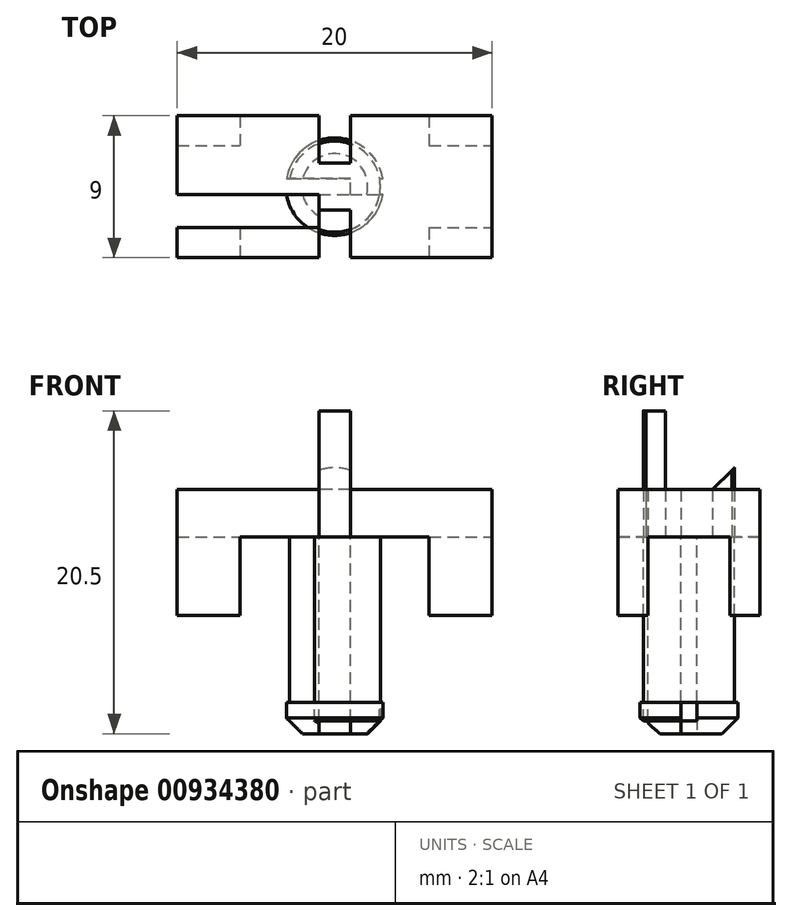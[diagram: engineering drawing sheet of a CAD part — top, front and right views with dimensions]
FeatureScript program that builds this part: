
annotation { "Feature Type Name" : "Feature", "Feature Type Description" : "" }
export const myFeature = defineFeature(function(context is Context, id is Id, definition is map)
    precondition{}
    {
        {
            var Q0;
            Q0=qCreatedBy(makeId("Top.planeOp"),FACE);
            var sketch = newSketch(context, id + "F0", { "sketchPlane" : qUnion([Q0])});
            skCircle(sketch, "E0", {"center": v(0, 0) * mm, "radius": 2.9 * mm});
            skLineSegment(sketch, "E1", {"start": v(-15.02, 0) * mm, "end": v(15.02, 0) * mm, "construction": true});
            skLineSegment(sketch, "E2.0", {"start": v(-15.02, -0.5) * mm, "end": v(15.02, -0.5) * mm});
            skLineSegment(sketch, "E3.0", {"start": v(-15.02, 0.5) * mm, "end": v(15.02, 0.5) * mm});
            skLineSegment(sketch, "E4.bottom", {"start": v(10, -4.5) * mm, "end": v(-10, -4.5) * mm});
            skLineSegment(sketch, "E4.top", {"start": v(10, 4.5) * mm, "end": v(-10, 4.5) * mm});
            skLineSegment(sketch, "E4.left", {"start": v(10, -4.5) * mm, "end": v(10, 4.5) * mm});
            skLineSegment(sketch, "E4.right", {"start": v(-10, -4.5) * mm, "end": v(-10, 4.5) * mm});
            skLineSegment(sketch, "E5.bottom", {"start": v(1, -4.5) * mm, "end": v(-1, -4.5) * mm});
            skLineSegment(sketch, "E5.top", {"start": v(1, 4.5) * mm, "end": v(-1, 4.5) * mm});
            skLineSegment(sketch, "E5.left", {"start": v(1, -4.5) * mm, "end": v(1, 4.5) * mm});
            skLineSegment(sketch, "E5.right", {"start": v(-1, -4.5) * mm, "end": v(-1, 4.5) * mm});
            skLineSegment(sketch, "E6", {"start": v(-1, 1.5) * mm, "end": v(1, 1.5) * mm});
            skLineSegment(sketch, "E7", {"start": v(-1, -1.5) * mm, "end": v(1, -1.5) * mm});
            skLineSegment(sketch, "E8", {"start": v(-10, 2.6) * mm, "end": v(10, 2.6) * mm});
            skLineSegment(sketch, "E9", {"start": v(-10, -2.6) * mm, "end": v(10, -2.6) * mm});
            skLineSegment(sketch, "E10", {"start": v(-6, 4.5) * mm, "end": v(-6, 2.6) * mm});
            skLineSegment(sketch, "E11", {"start": v(6, 4.5) * mm, "end": v(6, 2.6) * mm});
            skLineSegment(sketch, "E12", {"start": v(-6, -2.6) * mm, "end": v(-6, -4.5) * mm});
            skLineSegment(sketch, "E13", {"start": v(6, -2.6) * mm, "end": v(6, -4.5) * mm});
            skSolve(sketch);
        }
        {
            var Q0;
            {var subQ4=sQuery(id+"F0.wireOp",EDGE,"E8");var subQ6=sQuery(id+"F0.wireOp",EDGE,"E0");var subQ8=makeQuery(id+"F0.imprint","INTERSECT",VERTEX,{"disambiguationData":[OD(1.0)],"derivedFrom":[subQ6,subQ4]});Q0=makeQuery(id+"F0.imprint","IMPRINT",FACE,{"disambiguationData":[TD([[makeQuery(id+"F0.imprint","IMPRINT",EDGE,{"disambiguationData":[TD([[subQ8,-1.0]])],"derivedFrom":subQ6}),1.0]])]});}
            var Q1;
            {var subQ0=sQuery(id+"F0.wireOp",EDGE,"E6");Q1=makeQuery(id+"F0.imprint","IMPRINT",FACE,{"disambiguationData":[TD([[makeQuery(id+"F0.imprint","IMPRINT",EDGE,{"derivedFrom":subQ0}),1.0]])]});}
            var Q2;
            {var subQ5=sQuery(id+"F0.wireOp",EDGE,"E6");Q2=makeQuery(id+"F0.imprint","IMPRINT",FACE,{"disambiguationData":[TD([[makeQuery(id+"F0.imprint","IMPRINT",EDGE,{"derivedFrom":subQ5}),-1.0]])]});}
            var Q3;
            {var subQ2=sQuery(id+"F0.wireOp",EDGE,"E8");var subQ4=sQuery(id+"F0.wireOp",EDGE,"E0");var subQ5=makeQuery(id+"F0.imprint","INTERSECT",VERTEX,{"disambiguationData":[OD(0.0)],"derivedFrom":[subQ4,subQ2]});Q3=makeQuery(id+"F0.imprint","IMPRINT",FACE,{"disambiguationData":[TD([[makeQuery(id+"F0.imprint","IMPRINT",EDGE,{"disambiguationData":[TD([[subQ5,1.0]])],"derivedFrom":subQ4}),1.0]])]});}
            var Q4;
            {var subQ4=sQuery(id+"F0.wireOp",EDGE,"E9");var subQ6=sQuery(id+"F0.wireOp",EDGE,"E0");var subQ8=makeQuery(id+"F0.imprint","INTERSECT",VERTEX,{"disambiguationData":[OD(1.0)],"derivedFrom":[subQ6,subQ4]});Q4=makeQuery(id+"F0.imprint","IMPRINT",FACE,{"disambiguationData":[TD([[makeQuery(id+"F0.imprint","IMPRINT",EDGE,{"disambiguationData":[TD([[subQ8,-1.0]])],"derivedFrom":subQ6}),1.0]])]});}
            var Q5;
            {var subQ0=sQuery(id+"F0.wireOp",EDGE,"E7");Q5=makeQuery(id+"F0.imprint","IMPRINT",FACE,{"disambiguationData":[TD([[makeQuery(id+"F0.imprint","IMPRINT",EDGE,{"derivedFrom":subQ0}),-1.0]])]});}
            var Q6;
            {var subQ5=sQuery(id+"F0.wireOp",EDGE,"E7");Q6=makeQuery(id+"F0.imprint","IMPRINT",FACE,{"disambiguationData":[TD([[makeQuery(id+"F0.imprint","IMPRINT",EDGE,{"derivedFrom":subQ5}),1.0]])]});}
            var Q7;
            {var subQ2=sQuery(id+"F0.wireOp",EDGE,"E2.0");var subQ4=sQuery(id+"F0.wireOp",EDGE,"E0");var subQ5=makeQuery(id+"F0.imprint","INTERSECT",VERTEX,{"disambiguationData":[OD(0.0)],"derivedFrom":[subQ4,subQ2]});Q7=makeQuery(id+"F0.imprint","IMPRINT",FACE,{"disambiguationData":[TD([[makeQuery(id+"F0.imprint","IMPRINT",EDGE,{"disambiguationData":[TD([[subQ5,-1.0]])],"derivedFrom":subQ4}),1.0]])]});}
            var Q8;
            {var subQ0=sQuery(id+"F0.wireOp",EDGE,"E5.right");var subQ1=sQuery(id+"F0.wireOp",EDGE,"E0");var subQ2=makeQuery(id+"F0.imprint","INTERSECT",VERTEX,{"disambiguationData":[OD(1.0)],"derivedFrom":[subQ1,subQ0]});Q8=makeQuery(id+"F0.imprint","IMPRINT",FACE,{"disambiguationData":[TD([[makeQuery(id+"F0.imprint","IMPRINT",EDGE,{"disambiguationData":[TD([[subQ2,-1.0]])],"derivedFrom":subQ1}),1.0]])]});}
            var Q9;
            {var subQ0=sQuery(id+"F0.wireOp",EDGE,"E5.left");var subQ1=sQuery(id+"F0.wireOp",EDGE,"E0");var subQ2=makeQuery(id+"F0.imprint","INTERSECT",VERTEX,{"disambiguationData":[OD(0.0)],"derivedFrom":[subQ1,subQ0]});Q9=makeQuery(id+"F0.imprint","IMPRINT",FACE,{"disambiguationData":[TD([[makeQuery(id+"F0.imprint","IMPRINT",EDGE,{"disambiguationData":[TD([[subQ2,-1.0]])],"derivedFrom":subQ1}),1.0]])]});}
            var Q10;
            {var subQ0=sQuery(id+"F0.wireOp",EDGE,"E9");var subQ1=sQuery(id+"F0.wireOp",EDGE,"E0");var subQ2=makeQuery(id+"F0.imprint","INTERSECT",VERTEX,{"disambiguationData":[OD(0.0)],"derivedFrom":[subQ1,subQ0]});Q10=makeQuery(id+"F0.imprint","IMPRINT",FACE,{"disambiguationData":[TD([[makeQuery(id+"F0.imprint","IMPRINT",EDGE,{"disambiguationData":[TD([[subQ2,-1.0]])],"derivedFrom":subQ1}),1.0]])]});}
            var Q11;
            {var subQ0=sQuery(id+"F0.wireOp",EDGE,"E5.left");var subQ1=sQuery(id+"F0.wireOp",EDGE,"E0");var subQ2=makeQuery(id+"F0.imprint","INTERSECT",VERTEX,{"disambiguationData":[OD(1.0)],"derivedFrom":[subQ1,subQ0]});Q11=makeQuery(id+"F0.imprint","IMPRINT",FACE,{"disambiguationData":[TD([[makeQuery(id+"F0.imprint","IMPRINT",EDGE,{"disambiguationData":[TD([[subQ2,-1.0]])],"derivedFrom":subQ1}),1.0]])]});}
            var Q12;
            {var subQ0=sQuery(id+"F0.wireOp",EDGE,"E5.right");var subQ1=sQuery(id+"F0.wireOp",EDGE,"E0");var subQ2=makeQuery(id+"F0.imprint","INTERSECT",VERTEX,{"disambiguationData":[OD(0.0)],"derivedFrom":[subQ1,subQ0]});Q12=makeQuery(id+"F0.imprint","IMPRINT",FACE,{"disambiguationData":[TD([[makeQuery(id+"F0.imprint","IMPRINT",EDGE,{"disambiguationData":[TD([[subQ2,-1.0]])],"derivedFrom":subQ1}),1.0]])]});}
            var Q13;
            {var subQ0=sQuery(id+"F0.wireOp",EDGE,"E8");var subQ1=sQuery(id+"F0.wireOp",EDGE,"E0");var subQ2=makeQuery(id+"F0.imprint","INTERSECT",VERTEX,{"disambiguationData":[OD(0.0)],"derivedFrom":[subQ1,subQ0]});Q13=makeQuery(id+"F0.imprint","IMPRINT",FACE,{"disambiguationData":[TD([[makeQuery(id+"F0.imprint","IMPRINT",EDGE,{"disambiguationData":[TD([[subQ2,-1.0]])],"derivedFrom":subQ1}),1.0]])]});}
            extrude(context, id + "F1", {"entities" : qUnion([Q0, Q1, Q2, Q3, Q4, Q5, Q6, Q7, Q8, Q9, Q10, Q11, Q12, Q13]), "oppositeDirection" : true, "depth" : 10.5 * mm, "offsetDistance" : 25 * mm});
        }
        {
            var Q0;
            {var subQ5=sQuery(id+"F0.wireOp",EDGE,"E5.top");Q0=makeQuery(id+"F0.imprint","IMPRINT",FACE,{"disambiguationData":[TD([[makeQuery(id+"F0.imprint","IMPRINT",EDGE,{"derivedFrom":subQ5}),1.0]])]});}
            var Q1;
            {var subQ0=sQuery(id+"F0.wireOp",EDGE,"E6");Q1=makeQuery(id+"F0.imprint","IMPRINT",FACE,{"disambiguationData":[TD([[makeQuery(id+"F0.imprint","IMPRINT",EDGE,{"derivedFrom":subQ0}),1.0]])]});}
            var Q2;
            {var subQ0=sQuery(id+"F0.wireOp",EDGE,"E5.left");var subQ1=sQuery(id+"F0.wireOp",EDGE,"E0");var subQ2=makeQuery(id+"F0.imprint","INTERSECT",VERTEX,{"disambiguationData":[OD(0.0)],"derivedFrom":[subQ1,subQ0]});Q2=makeQuery(id+"F0.imprint","IMPRINT",FACE,{"disambiguationData":[TD([[makeQuery(id+"F0.imprint","IMPRINT",EDGE,{"disambiguationData":[TD([[subQ2,-1.0]])],"derivedFrom":subQ1}),1.0]])]});}
            var Q3;
            {var subQ0=sQuery(id+"F0.wireOp",EDGE,"E7");Q3=makeQuery(id+"F0.imprint","IMPRINT",FACE,{"disambiguationData":[TD([[makeQuery(id+"F0.imprint","IMPRINT",EDGE,{"derivedFrom":subQ0}),-1.0]])]});}
            var Q4;
            {var subQ0=sQuery(id+"F0.wireOp",EDGE,"E5.right");var subQ1=sQuery(id+"F0.wireOp",EDGE,"E0");var subQ2=makeQuery(id+"F0.imprint","INTERSECT",VERTEX,{"disambiguationData":[OD(1.0)],"derivedFrom":[subQ1,subQ0]});Q4=makeQuery(id+"F0.imprint","IMPRINT",FACE,{"disambiguationData":[TD([[makeQuery(id+"F0.imprint","IMPRINT",EDGE,{"disambiguationData":[TD([[subQ2,-1.0]])],"derivedFrom":subQ1}),1.0]])]});}
            var Q5;
            {var subQ5=sQuery(id+"F0.wireOp",EDGE,"E5.bottom");Q5=makeQuery(id+"F0.imprint","IMPRINT",FACE,{"disambiguationData":[TD([[makeQuery(id+"F0.imprint","IMPRINT",EDGE,{"derivedFrom":subQ5}),-1.0]])]});}
            extrude(context, id + "F2", {"entities" : qUnion([Q0, Q1, Q2, Q3, Q4, Q5]), "depth" : 8 * mm, "offsetDistance" : 25 * mm});
        }
        {
            var Q0;
            {var subQ0=sQuery(id+"F0.wireOp",EDGE,"E5.right");var subQ3=sQuery(id+"F0.wireOp",EDGE,"E0");var subQ4=makeQuery(id+"F0.imprint","INTERSECT",VERTEX,{"disambiguationData":[OD(0.0)],"derivedFrom":[subQ3,subQ0]});Q0=makeQuery(id+"F0.imprint","IMPRINT",FACE,{"disambiguationData":[TD([[makeQuery(id+"F0.imprint","IMPRINT",EDGE,{"disambiguationData":[TD([[subQ4,-1.0]])],"derivedFrom":subQ3}),-1.0]])]});}
            var Q1;
            {var subQ0=sQuery(id+"F0.wireOp",EDGE,"E8");var subQ1=sQuery(id+"F0.wireOp",EDGE,"E0");var subQ2=makeQuery(id+"F0.imprint","INTERSECT",VERTEX,{"disambiguationData":[OD(1.0)],"derivedFrom":[subQ1,subQ0]});Q1=makeQuery(id+"F0.imprint","IMPRINT",FACE,{"disambiguationData":[TD([[makeQuery(id+"F0.imprint","IMPRINT",EDGE,{"disambiguationData":[TD([[subQ2,-1.0]])],"derivedFrom":subQ1}),-1.0]])]});}
            var Q2;
            {var subQ4=sQuery(id+"F0.wireOp",EDGE,"E8");var subQ6=sQuery(id+"F0.wireOp",EDGE,"E0");var subQ8=makeQuery(id+"F0.imprint","INTERSECT",VERTEX,{"disambiguationData":[OD(1.0)],"derivedFrom":[subQ6,subQ4]});Q2=makeQuery(id+"F0.imprint","IMPRINT",FACE,{"disambiguationData":[TD([[makeQuery(id+"F0.imprint","IMPRINT",EDGE,{"disambiguationData":[TD([[subQ8,-1.0]])],"derivedFrom":subQ6}),1.0]])]});}
            var Q3;
            {var subQ0=sQuery(id+"F0.wireOp",EDGE,"E3.0");var subQ1=sQuery(id+"F0.wireOp",EDGE,"E0");var subQ2=makeQuery(id+"F0.imprint","INTERSECT",VERTEX,{"disambiguationData":[OD(1.0)],"derivedFrom":[subQ1,subQ0]});Q3=makeQuery(id+"F0.imprint","IMPRINT",FACE,{"disambiguationData":[TD([[makeQuery(id+"F0.imprint","IMPRINT",EDGE,{"disambiguationData":[TD([[subQ2,-1.0]])],"derivedFrom":subQ1}),-1.0]])]});}
            var Q4;
            {var subQ0=sQuery(id+"F0.wireOp",EDGE,"E3.0");var subQ1=sQuery(id+"F0.wireOp",EDGE,"E0");var subQ2=makeQuery(id+"F0.imprint","INTERSECT",VERTEX,{"disambiguationData":[OD(1.0)],"derivedFrom":[subQ1,subQ0]});Q4=makeQuery(id+"F0.imprint","IMPRINT",FACE,{"disambiguationData":[TD([[makeQuery(id+"F0.imprint","IMPRINT",EDGE,{"disambiguationData":[TD([[subQ2,-1.0]])],"derivedFrom":subQ1}),1.0]])]});}
            var Q5;
            {var subQ2=sQuery(id+"F0.wireOp",EDGE,"E2.0");var subQ4=sQuery(id+"F0.wireOp",EDGE,"E0");var subQ5=makeQuery(id+"F0.imprint","INTERSECT",VERTEX,{"disambiguationData":[OD(0.0)],"derivedFrom":[subQ4,subQ2]});Q5=makeQuery(id+"F0.imprint","IMPRINT",FACE,{"disambiguationData":[TD([[makeQuery(id+"F0.imprint","IMPRINT",EDGE,{"disambiguationData":[TD([[subQ5,-1.0]])],"derivedFrom":subQ4}),1.0]])]});}
            var Q6;
            {var subQ0=sQuery(id+"F0.wireOp",EDGE,"E2.0");var subQ1=sQuery(id+"F0.wireOp",EDGE,"E0");var subQ2=makeQuery(id+"F0.imprint","INTERSECT",VERTEX,{"disambiguationData":[OD(0.0)],"derivedFrom":[subQ1,subQ0]});Q6=makeQuery(id+"F0.imprint","IMPRINT",FACE,{"disambiguationData":[TD([[makeQuery(id+"F0.imprint","IMPRINT",EDGE,{"disambiguationData":[TD([[subQ2,-1.0]])],"derivedFrom":subQ1}),-1.0]])]});}
            var Q7;
            {var subQ3=sQuery(id+"F0.wireOp",EDGE,"E9");var subQ7=sQuery(id+"F0.wireOp",EDGE,"E0");var subQ9=makeQuery(id+"F0.imprint","INTERSECT",VERTEX,{"disambiguationData":[OD(0.0)],"derivedFrom":[subQ7,subQ3]});Q7=makeQuery(id+"F0.imprint","IMPRINT",FACE,{"disambiguationData":[TD([[makeQuery(id+"F0.imprint","IMPRINT",EDGE,{"disambiguationData":[TD([[subQ9,-1.0]])],"derivedFrom":subQ7}),-1.0]])]});}
            var Q8;
            {var subQ5=sQuery(id+"F0.wireOp",EDGE,"E6");Q8=makeQuery(id+"F0.imprint","IMPRINT",FACE,{"disambiguationData":[TD([[makeQuery(id+"F0.imprint","IMPRINT",EDGE,{"derivedFrom":subQ5}),-1.0]])]});}
            var Q9;
            {var subQ0=sQuery(id+"F0.wireOp",EDGE,"E5.right");var subQ1=sQuery(id+"F0.wireOp",EDGE,"E2.0");var subQ2=makeQuery(id+"F0.imprint","INTERSECT",VERTEX,{"derivedFrom":[subQ1,subQ0]});Q9=makeQuery(id+"F0.imprint","IMPRINT",FACE,{"disambiguationData":[TD([[makeQuery(id+"F0.imprint","IMPRINT",EDGE,{"disambiguationData":[TD([[subQ2,-1.0]])],"derivedFrom":subQ1}),1.0]])]});}
            var Q10;
            {var subQ5=sQuery(id+"F0.wireOp",EDGE,"E7");Q10=makeQuery(id+"F0.imprint","IMPRINT",FACE,{"disambiguationData":[TD([[makeQuery(id+"F0.imprint","IMPRINT",EDGE,{"derivedFrom":subQ5}),1.0]])]});}
            var Q11;
            {var subQ3=sQuery(id+"F0.wireOp",EDGE,"E8");var subQ7=sQuery(id+"F0.wireOp",EDGE,"E0");var subQ9=makeQuery(id+"F0.imprint","INTERSECT",VERTEX,{"disambiguationData":[OD(0.0)],"derivedFrom":[subQ7,subQ3]});Q11=makeQuery(id+"F0.imprint","IMPRINT",FACE,{"disambiguationData":[TD([[makeQuery(id+"F0.imprint","IMPRINT",EDGE,{"disambiguationData":[TD([[subQ9,-1.0]])],"derivedFrom":subQ7}),-1.0]])]});}
            var Q12;
            {var subQ2=sQuery(id+"F0.wireOp",EDGE,"E8");var subQ4=sQuery(id+"F0.wireOp",EDGE,"E0");var subQ5=makeQuery(id+"F0.imprint","INTERSECT",VERTEX,{"disambiguationData":[OD(0.0)],"derivedFrom":[subQ4,subQ2]});Q12=makeQuery(id+"F0.imprint","IMPRINT",FACE,{"disambiguationData":[TD([[makeQuery(id+"F0.imprint","IMPRINT",EDGE,{"disambiguationData":[TD([[subQ5,1.0]])],"derivedFrom":subQ4}),1.0]])]});}
            var Q13;
            {var subQ0=sQuery(id+"F0.wireOp",EDGE,"E8");var subQ1=sQuery(id+"F0.wireOp",EDGE,"E0");var subQ2=makeQuery(id+"F0.imprint","INTERSECT",VERTEX,{"disambiguationData":[OD(0.0)],"derivedFrom":[subQ1,subQ0]});Q13=makeQuery(id+"F0.imprint","IMPRINT",FACE,{"disambiguationData":[TD([[makeQuery(id+"F0.imprint","IMPRINT",EDGE,{"disambiguationData":[TD([[subQ2,-1.0]])],"derivedFrom":subQ1}),1.0]])]});}
            var Q14;
            {var subQ0=sQuery(id+"F0.wireOp",EDGE,"E8");var subQ1=sQuery(id+"F0.wireOp",EDGE,"E0");var subQ2=makeQuery(id+"F0.imprint","INTERSECT",VERTEX,{"disambiguationData":[OD(0.0)],"derivedFrom":[subQ1,subQ0]});Q14=makeQuery(id+"F0.imprint","IMPRINT",FACE,{"disambiguationData":[TD([[makeQuery(id+"F0.imprint","IMPRINT",EDGE,{"disambiguationData":[TD([[subQ2,1.0]])],"derivedFrom":subQ1}),-1.0]])]});}
            var Q15;
            {var subQ0=sQuery(id+"F0.wireOp",EDGE,"E3.0");var subQ1=sQuery(id+"F0.wireOp",EDGE,"E0");var subQ2=makeQuery(id+"F0.imprint","INTERSECT",VERTEX,{"disambiguationData":[OD(0.0)],"derivedFrom":[subQ1,subQ0]});Q15=makeQuery(id+"F0.imprint","IMPRINT",FACE,{"disambiguationData":[TD([[makeQuery(id+"F0.imprint","IMPRINT",EDGE,{"disambiguationData":[TD([[subQ2,1.0]])],"derivedFrom":subQ1}),-1.0]])]});}
            var Q16;
            {var subQ0=sQuery(id+"F0.wireOp",EDGE,"E3.0");var subQ1=sQuery(id+"F0.wireOp",EDGE,"E0");var subQ2=makeQuery(id+"F0.imprint","INTERSECT",VERTEX,{"disambiguationData":[OD(0.0)],"derivedFrom":[subQ1,subQ0]});Q16=makeQuery(id+"F0.imprint","IMPRINT",FACE,{"disambiguationData":[TD([[makeQuery(id+"F0.imprint","IMPRINT",EDGE,{"disambiguationData":[TD([[subQ2,1.0]])],"derivedFrom":subQ1}),1.0]])]});}
            var Q17;
            {var subQ4=sQuery(id+"F0.wireOp",EDGE,"E9");var subQ6=sQuery(id+"F0.wireOp",EDGE,"E0");var subQ8=makeQuery(id+"F0.imprint","INTERSECT",VERTEX,{"disambiguationData":[OD(1.0)],"derivedFrom":[subQ6,subQ4]});Q17=makeQuery(id+"F0.imprint","IMPRINT",FACE,{"disambiguationData":[TD([[makeQuery(id+"F0.imprint","IMPRINT",EDGE,{"disambiguationData":[TD([[subQ8,-1.0]])],"derivedFrom":subQ6}),1.0]])]});}
            var Q18;
            {var subQ0=sQuery(id+"F0.wireOp",EDGE,"E9");var subQ1=sQuery(id+"F0.wireOp",EDGE,"E0");var subQ2=makeQuery(id+"F0.imprint","INTERSECT",VERTEX,{"disambiguationData":[OD(1.0)],"derivedFrom":[subQ1,subQ0]});Q18=makeQuery(id+"F0.imprint","IMPRINT",FACE,{"disambiguationData":[TD([[makeQuery(id+"F0.imprint","IMPRINT",EDGE,{"disambiguationData":[TD([[subQ2,-1.0]])],"derivedFrom":subQ1}),-1.0]])]});}
            var Q19;
            {var subQ0=sQuery(id+"F0.wireOp",EDGE,"E5.left");var subQ1=sQuery(id+"F0.wireOp",EDGE,"E0");var subQ2=makeQuery(id+"F0.imprint","INTERSECT",VERTEX,{"disambiguationData":[OD(1.0)],"derivedFrom":[subQ1,subQ0]});Q19=makeQuery(id+"F0.imprint","IMPRINT",FACE,{"disambiguationData":[TD([[makeQuery(id+"F0.imprint","IMPRINT",EDGE,{"disambiguationData":[TD([[subQ2,-1.0]])],"derivedFrom":subQ1}),1.0]])]});}
            var Q20;
            {var subQ0=sQuery(id+"F0.wireOp",EDGE,"E5.left");var subQ3=sQuery(id+"F0.wireOp",EDGE,"E0");var subQ4=makeQuery(id+"F0.imprint","INTERSECT",VERTEX,{"disambiguationData":[OD(1.0)],"derivedFrom":[subQ3,subQ0]});Q20=makeQuery(id+"F0.imprint","IMPRINT",FACE,{"disambiguationData":[TD([[makeQuery(id+"F0.imprint","IMPRINT",EDGE,{"disambiguationData":[TD([[subQ4,-1.0]])],"derivedFrom":subQ3}),-1.0]])]});}
            var Q21;
            {var subQ0=sQuery(id+"F0.wireOp",EDGE,"E9");var subQ1=sQuery(id+"F0.wireOp",EDGE,"E0");var subQ2=makeQuery(id+"F0.imprint","INTERSECT",VERTEX,{"disambiguationData":[OD(0.0)],"derivedFrom":[subQ1,subQ0]});Q21=makeQuery(id+"F0.imprint","IMPRINT",FACE,{"disambiguationData":[TD([[makeQuery(id+"F0.imprint","IMPRINT",EDGE,{"disambiguationData":[TD([[subQ2,-1.0]])],"derivedFrom":subQ1}),1.0]])]});}
            var Q22;
            {var subQ0=sQuery(id+"F0.wireOp",EDGE,"E5.right");var subQ1=sQuery(id+"F0.wireOp",EDGE,"E0");var subQ2=makeQuery(id+"F0.imprint","INTERSECT",VERTEX,{"disambiguationData":[OD(0.0)],"derivedFrom":[subQ1,subQ0]});Q22=makeQuery(id+"F0.imprint","IMPRINT",FACE,{"disambiguationData":[TD([[makeQuery(id+"F0.imprint","IMPRINT",EDGE,{"disambiguationData":[TD([[subQ2,-1.0]])],"derivedFrom":subQ1}),1.0]])]});}
            var Q23;
            {var subQ3=sQuery(id+"F0.wireOp",EDGE,"E10");Q23=makeQuery(id+"F0.imprint","IMPRINT",FACE,{"disambiguationData":[TD([[makeQuery(id+"F0.imprint","IMPRINT",EDGE,{"derivedFrom":subQ3}),-1.0]])]});}
            var Q24;
            {var subQ3=sQuery(id+"F0.wireOp",EDGE,"E12");Q24=makeQuery(id+"F0.imprint","IMPRINT",FACE,{"disambiguationData":[TD([[makeQuery(id+"F0.imprint","IMPRINT",EDGE,{"derivedFrom":subQ3}),-1.0]])]});}
            var Q25;
            {var subQ3=sQuery(id+"F0.wireOp",EDGE,"E11");Q25=makeQuery(id+"F0.imprint","IMPRINT",FACE,{"disambiguationData":[TD([[makeQuery(id+"F0.imprint","IMPRINT",EDGE,{"derivedFrom":subQ3}),1.0]])]});}
            var Q26;
            {var subQ3=sQuery(id+"F0.wireOp",EDGE,"E13");Q26=makeQuery(id+"F0.imprint","IMPRINT",FACE,{"disambiguationData":[TD([[makeQuery(id+"F0.imprint","IMPRINT",EDGE,{"derivedFrom":subQ3}),1.0]])]});}
            extrude(context, id + "F3", {"entities" : qUnion([Q0, Q1, Q2, Q3, Q4, Q5, Q6, Q7, Q8, Q9, Q10, Q11, Q12, Q13, Q14, Q15, Q16, Q17, Q18, Q19, Q20, Q21, Q22, Q23, Q24, Q25, Q26]), "depth" : 3 * mm, "offsetDistance" : 25 * mm});
        }
        {
            var Q0;
            {var subQ3=sQuery(id+"F0.wireOp",EDGE,"E12");Q0=makeQuery(id+"F0.imprint","IMPRINT",FACE,{"disambiguationData":[TD([[makeQuery(id+"F0.imprint","IMPRINT",EDGE,{"derivedFrom":subQ3}),-1.0]])]});}
            var Q1;
            {var subQ3=sQuery(id+"F0.wireOp",EDGE,"E10");Q1=makeQuery(id+"F0.imprint","IMPRINT",FACE,{"disambiguationData":[TD([[makeQuery(id+"F0.imprint","IMPRINT",EDGE,{"derivedFrom":subQ3}),-1.0]])]});}
            var Q2;
            {var subQ3=sQuery(id+"F0.wireOp",EDGE,"E13");Q2=makeQuery(id+"F0.imprint","IMPRINT",FACE,{"disambiguationData":[TD([[makeQuery(id+"F0.imprint","IMPRINT",EDGE,{"derivedFrom":subQ3}),1.0]])]});}
            var Q3;
            {var subQ3=sQuery(id+"F0.wireOp",EDGE,"E11");Q3=makeQuery(id+"F0.imprint","IMPRINT",FACE,{"disambiguationData":[TD([[makeQuery(id+"F0.imprint","IMPRINT",EDGE,{"derivedFrom":subQ3}),1.0]])]});}
            extrude(context, id + "F4", {"entities" : qUnion([Q0, Q1, Q2, Q3]), "operationType" : NewBodyOperationType.ADD, "oppositeDirection" : true, "depth" : 5 * mm, "offsetDistance" : 25 * mm});
        }
        {
            var Q0;
            Q0=makeQuery(id+"F2.opExtrude","CAP_EDGE",EDGE,{"disambiguationData":[OSD([sQuery(id+"F0.wireOp",EDGE,"E6")])],"isStart":false});
            chamfer(context, id + "F5", {"entities" : qUnion([Q0]), "width" : 5 * mm, "tangentPropagation" : true});
        }
        {
            var Q0;
            Q0=makeQuery(id+"F1.opExtrude","CAP_FACE",FACE,{"disambiguationData":[OSD([sQuery(id+"F0.wireOp",EDGE,"E0"),sQuery(id+"F0.wireOp",EDGE,"E3.0")])],"isStart":false});
            var sketch = newSketch(context, id + "F6", { "sketchPlane" : qUnion([Q0])});
            skCircle(sketch, "E14", {"center": v(0, 0) * mm, "radius": 3.1 * mm});
            skPoint(sketch, "E15", {"position": v(0, 0.5) * mm});
            skPoint(sketch, "E16", {"position": v(0, -0.5) * mm});
            skLineSegment(sketch, "E17", {"start": v(0, 0.5) * mm, "end": v(-3.06, 0.5) * mm});
            skLineSegment(sketch, "E18", {"start": v(0, 0.5) * mm, "end": v(3.06, 0.5) * mm});
            skLineSegment(sketch, "E19", {"start": v(0, -0.5) * mm, "end": v(-3.06, -0.5) * mm});
            skLineSegment(sketch, "E20", {"start": v(0, -0.5) * mm, "end": v(3.06, -0.5) * mm});
            skSolve(sketch);
        }
        {
            var Q0;
            {var subQ0=sQuery(id+"F6.wireOp",EDGE,"E17");Q0=makeQuery(id+"F6.imprint","IMPRINT",FACE,{"disambiguationData":[TD([[makeQuery(id+"F6.imprint","IMPRINT",EDGE,{"derivedFrom":subQ0}),-1.0]])]});}
            var Q1;
            {var subQ0=sQuery(id+"F6.wireOp",EDGE,"E19");var subQ1=sQuery(id+"F6.wireOp",EDGE,"E14");var subQ2=makeQuery(id+"F6.imprint","INTERSECT",VERTEX,{"derivedFrom":[subQ1,subQ0]});Q1=makeQuery(id+"F6.imprint","IMPRINT",FACE,{"disambiguationData":[TD([[makeQuery(id+"F6.imprint","IMPRINT",EDGE,{"disambiguationData":[TD([[subQ2,-1.0]])],"derivedFrom":subQ1}),1.0]])]});}
            var Q2;
            {var subQ1=sQuery(id+"F0.wireOp",EDGE,"E8");var subQ2=sQuery(id+"F0.wireOp",EDGE,"E0");var subQ3=makeQuery(id+"F0.imprint","INTERSECT",VERTEX,{"disambiguationData":[OD(1.0)],"derivedFrom":[subQ2,subQ1]});var subQ5=makeQuery(id+"F0.imprint","INTERSECT",VERTEX,{"disambiguationData":[OD(0.0)],"derivedFrom":[subQ2,sQuery(id+"F0.wireOp",EDGE,"E5.right")]});var subQ6=makeQuery(id+"F0.imprint","INTERSECT",VERTEX,{"disambiguationData":[OD(0.0)],"derivedFrom":[subQ2,sQuery(id+"F0.wireOp",EDGE,"E5.left")]});var subQ7=makeQuery(id+"F0.imprint","INTERSECT",VERTEX,{"disambiguationData":[OD(0.0)],"derivedFrom":[subQ2,subQ1]});var subQ8=makeQuery(id+"F1.opExtrude","CAP_EDGE",EDGE,{"disambiguationData":[OSD([subQ2]),TDD([makeQuery(id+"F0.imprint","IMPRINT",EDGE,{"disambiguationData":[TD([[subQ7,1.0]])],"derivedFrom":subQ2}),makeQuery(id+"F0.imprint","IMPRINT",EDGE,{"disambiguationData":[TD([[subQ7,-1.0]])],"derivedFrom":subQ2}),makeQuery(id+"F0.imprint","IMPRINT",EDGE,{"disambiguationData":[TD([[subQ6,-1.0]])],"derivedFrom":subQ2}),makeQuery(id+"F0.imprint","IMPRINT",EDGE,{"disambiguationData":[TD([[subQ5,-1.0]])],"derivedFrom":subQ2}),makeQuery(id+"F0.imprint","IMPRINT",EDGE,{"disambiguationData":[TD([[subQ3,-1.0]])],"derivedFrom":subQ2})])],"isStart":false});Q2=makeQuery(id+"F6.imprint","IMPRINT",FACE,{"disambiguationData":[TD([[makeQuery(id+"F6.imprint","IMPRINT",EDGE,{"derivedFrom":subQ8}),-1.0]])]});}
            extrude(context, id + "F7", {"entities" : qUnion([Q0, Q1, Q2]), "depth" : 2 * mm, "offsetDistance" : 25 * mm});
        }
        {
            var Q0;
            {var subQ0=sQuery(id+"F6.wireOp",EDGE,"E14");Q0=makeQuery(id+"F7.opExtrude","CAP_EDGE",EDGE,{"disambiguationData":[OSD([subQ0]),TDD([makeQuery(id+"F6.imprint","IMPRINT",EDGE,{"disambiguationData":[TD([[makeQuery(id+"F6.imprint","INTERSECT",VERTEX,{"derivedFrom":[subQ0,sQuery(id+"F6.wireOp",EDGE,"E19")]}),-1.0]])],"derivedFrom":subQ0})])],"isStart":false});}
            var Q1;
            {var subQ0=sQuery(id+"F6.wireOp",EDGE,"E14");Q1=makeQuery(id+"F7.opExtrude","CAP_EDGE",EDGE,{"disambiguationData":[OSD([subQ0]),TDD([makeQuery(id+"F6.imprint","IMPRINT",EDGE,{"disambiguationData":[TD([[makeQuery(id+"F6.imprint","INTERSECT",VERTEX,{"derivedFrom":[subQ0,sQuery(id+"F6.wireOp",EDGE,"E17")]}),1.0]])],"derivedFrom":subQ0})])],"isStart":false});}
            chamfer(context, id + "F8", {"entities" : qUnion([Q0, Q1]), "width" : 1 * mm, "tangentPropagation" : true});
        }
    });
